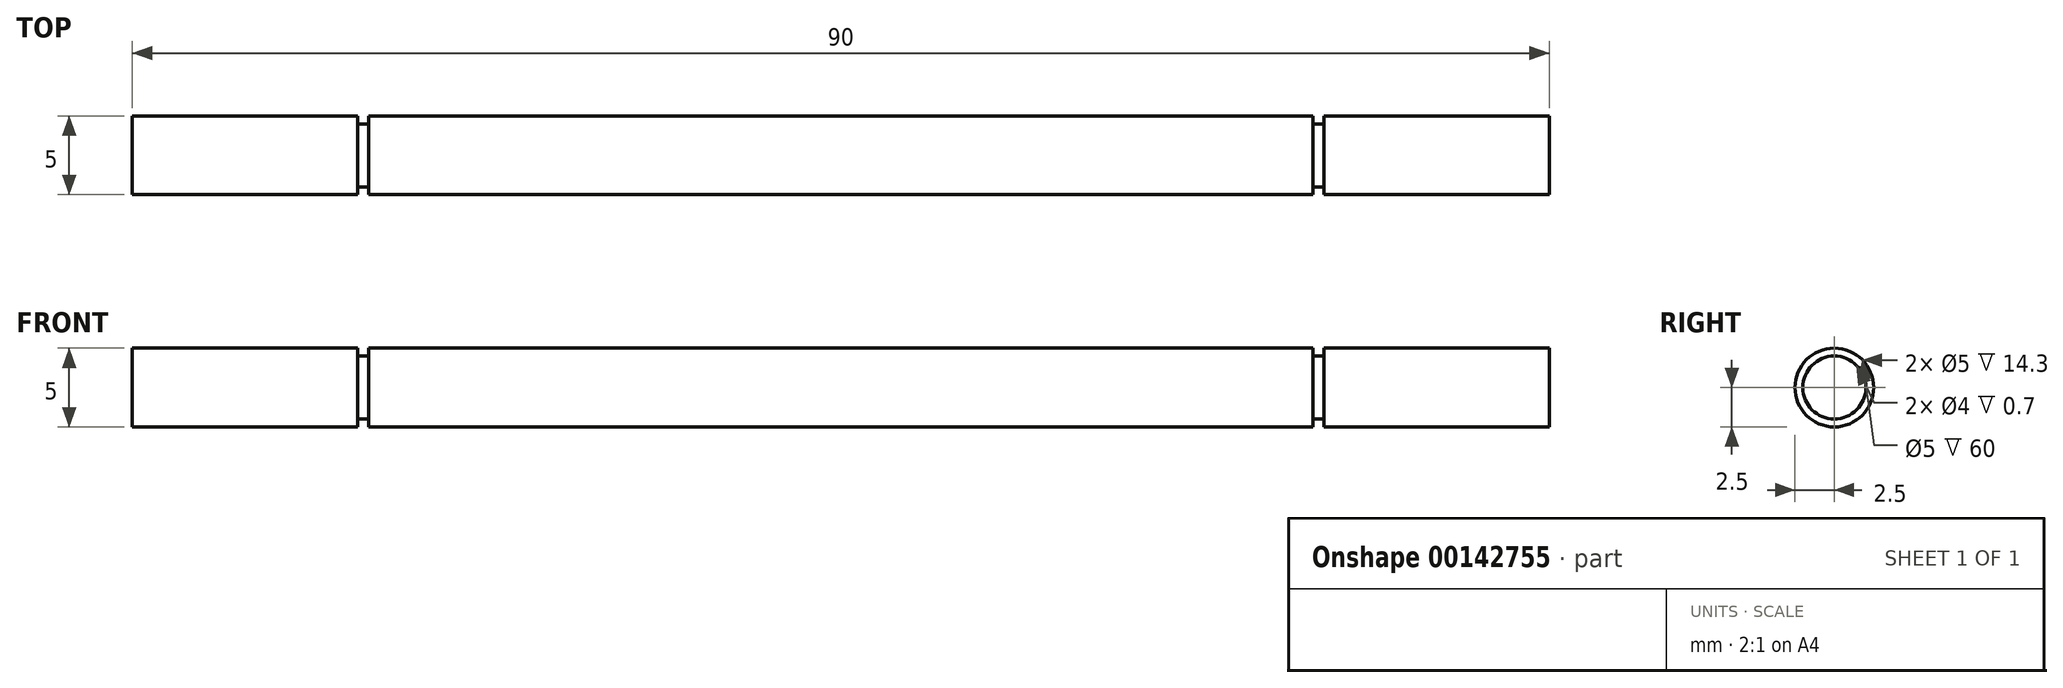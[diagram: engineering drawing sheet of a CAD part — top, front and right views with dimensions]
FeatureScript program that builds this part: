
annotation { "Feature Type Name" : "Feature", "Feature Type Description" : "" }
export const myFeature = defineFeature(function(context is Context, id is Id, definition is map)
    precondition{}
    {
        {
            var Q0;
            Q0=qCreatedBy(makeId("Front.planeOp"),FACE);
            var sketch = newSketch(context, id + "F0", { "sketchPlane" : qUnion([Q0])});
            skLineSegment(sketch, "E0", {"start": v(0, 0) * mm, "end": v(0, 2.5) * mm});
            skLineSegment(sketch, "E1", {"start": v(0, 0) * mm, "end": v(90, 0) * mm, "construction": true});
            skLineSegment(sketch, "E2", {"start": v(90, 0) * mm, "end": v(90, 2.5) * mm});
            skLineSegment(sketch, "E3", {"start": v(45, 2.5) * mm, "end": v(15, 2.5) * mm});
            skPoint(sketch, "E3.startSnap0", {"position": v(45, 0) * mm});
            skLineSegment(sketch, "E4", {"start": v(45, 2.5) * mm, "end": v(75, 2.5) * mm});
            skLineSegment(sketch, "E5", {"start": v(75, 2.5) * mm, "end": v(75, 2) * mm});
            skLineSegment(sketch, "E6", {"start": v(75, 2) * mm, "end": v(75.7, 2) * mm});
            skLineSegment(sketch, "E7", {"start": v(75.7, 2) * mm, "end": v(75.7, 2.5) * mm});
            skLineSegment(sketch, "E8", {"start": v(75.7, 2.5) * mm, "end": v(90, 2.5) * mm});
            skLineSegment(sketch, "E9", {"start": v(15, 2.5) * mm, "end": v(15, 2) * mm});
            skLineSegment(sketch, "E10", {"start": v(15, 2) * mm, "end": v(14.3, 2) * mm});
            skLineSegment(sketch, "E11", {"start": v(14.3, 2) * mm, "end": v(14.3, 2.5) * mm});
            skLineSegment(sketch, "E12", {"start": v(14.3, 2.5) * mm, "end": v(0, 2.5) * mm});
            skArc(sketch, "E13", {"start": v(46, 0) * mm, "mid": v(45, 1) * mm, "end": v(44, 0) * mm});
            skArc(sketch, "E14", {"start": v(2.5, 0) * mm, "mid": v(2, 0.5) * mm, "end": v(1.5, 0) * mm});
            skArc(sketch, "E15", {"start": v(88.5, 0) * mm, "mid": v(88, 0.5) * mm, "end": v(87.5, 0) * mm});
            skSolve(sketch);
        }
        {
            var Q0;
            Q0=sQuery(id+"F0.wireOp",EDGE,"E0");
            var Q1;
            Q1=sQuery(id+"F0.wireOp",EDGE,"E12");
            var Q2;
            Q2=sQuery(id+"F0.wireOp",EDGE,"E11");
            var Q3;
            Q3=sQuery(id+"F0.wireOp",EDGE,"E10");
            var Q4;
            Q4=sQuery(id+"F0.wireOp",EDGE,"E9");
            var Q5;
            Q5=sQuery(id+"F0.wireOp",EDGE,"E3");
            var Q6;
            Q6=sQuery(id+"F0.wireOp",EDGE,"E4");
            var Q7;
            Q7=sQuery(id+"F0.wireOp",EDGE,"E8");
            var Q8;
            Q8=sQuery(id+"F0.wireOp",EDGE,"E2");
            var Q9;
            Q9=sQuery(id+"F0.wireOp",EDGE,"E6");
            var Q10;
            Q10=sQuery(id+"F0.wireOp",EDGE,"E5");
            var Q11;
            Q11=sQuery(id+"F0.wireOp",EDGE,"E7");
            var Q12;
            Q12=sQuery(id+"F0.wireOp",EDGE,"E1");
            revolve(context, id + "F1", {"bodyType" : ToolBodyType.SURFACE, "surfaceEntities" : qUnion([Q0, Q1, Q2, Q3, Q4, Q5, Q6, Q7, Q8, Q9, Q10, Q11]), "axis" : qUnion([Q12]), "revolveType" : RevolveType.FULL});
        }
    });
